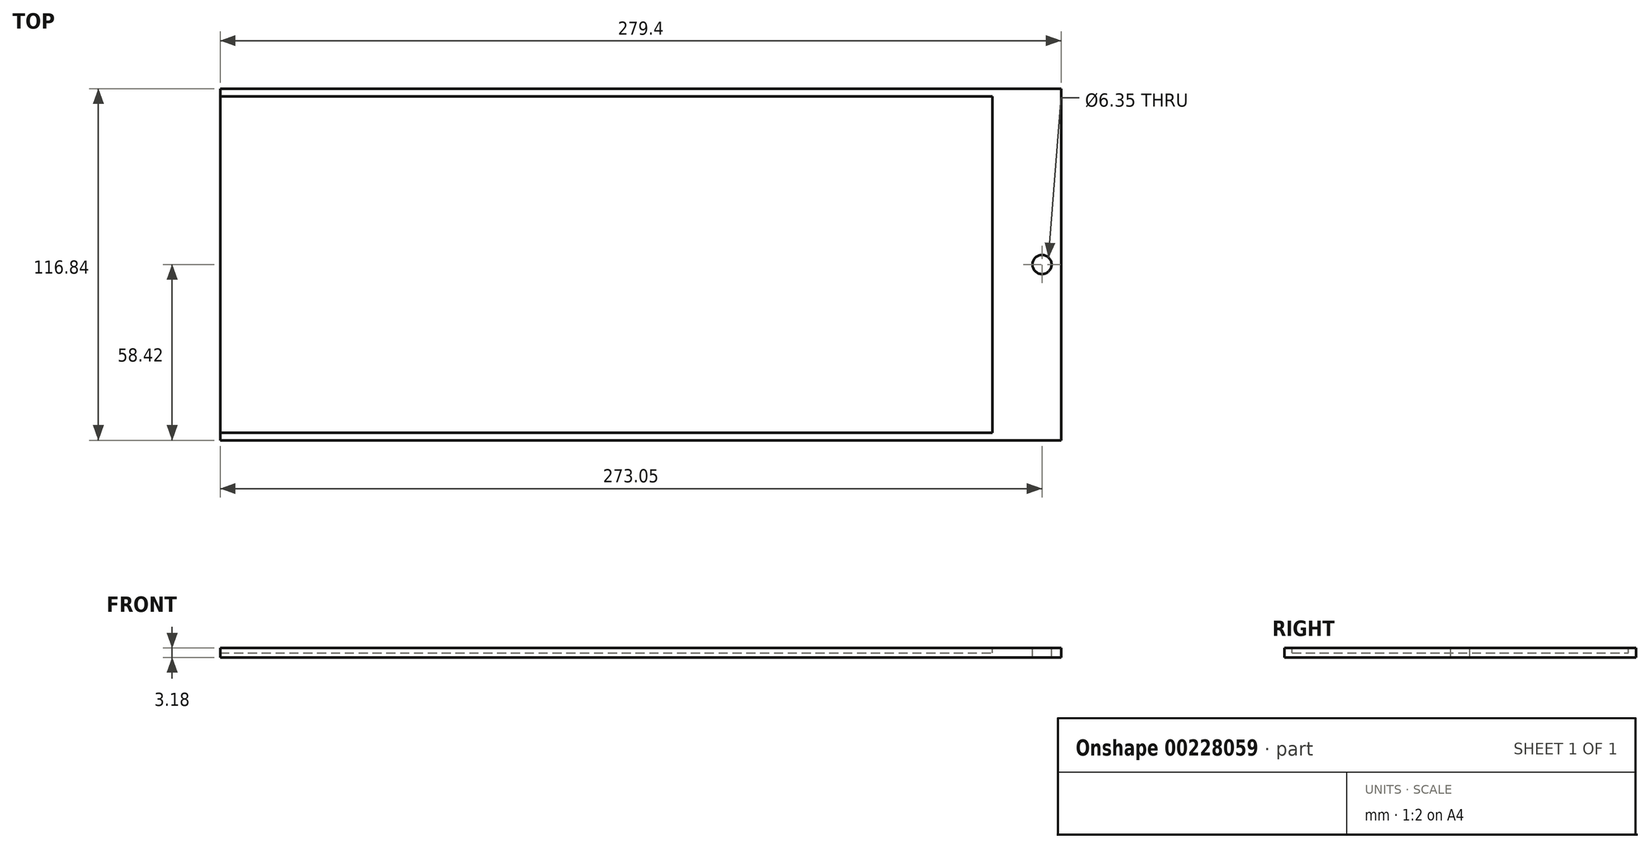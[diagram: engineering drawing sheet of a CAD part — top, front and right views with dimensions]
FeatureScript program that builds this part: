
annotation { "Feature Type Name" : "Feature", "Feature Type Description" : "" }
export const myFeature = defineFeature(function(context is Context, id is Id, definition is map)
    precondition{}
    {
        {
            var Q0;
            Q0=qCreatedBy(makeId("Top.planeOp"),FACE);
            var sketch = newSketch(context, id + "F0", { "sketchPlane" : qUnion([Q0])});
            skLineSegment(sketch, "E0.bottom", {"start": v(0, 0) * mm, "end": v(279.4, 0) * mm});
            skLineSegment(sketch, "E0.top", {"start": v(0, 116.84) * mm, "end": v(279.4, 116.84) * mm});
            skLineSegment(sketch, "E0.left", {"start": v(0, 0) * mm, "end": v(0, 116.84) * mm});
            skLineSegment(sketch, "E0.right", {"start": v(279.4, 0) * mm, "end": v(279.4, 116.84) * mm});
            skSolve(sketch);
        }
        {
            var Q0;
            Q0 = qSketchRegion(id + "F0", true);
            extrude(context, id + "F1", {"entities" : qUnion([Q0]), "depth" : 3.17 * mm, "offsetDistance" : 25.4 * mm});
        }
        {
            var Q0;
            Q0=makeQuery(id+"F1.opExtrude","CAP_FACE",FACE,{"disambiguationData":[OSD([sQuery(id+"F0.wireOp",EDGE,"E0.bottom"),sQuery(id+"F0.wireOp",EDGE,"E0.top"),sQuery(id+"F0.wireOp",EDGE,"E0.left"),sQuery(id+"F0.wireOp",EDGE,"E0.right")])],"isStart":false});
            var sketch = newSketch(context, id + "F2", { "sketchPlane" : qUnion([Q0])});
            skCircle(sketch, "E1", {"center": v(273.05, 58.42) * mm, "radius": 3.18 * mm});
            skLineSegment(sketch, "E2", {"start": v(279.4, 58.42) * mm, "end": v(0, 58.42) * mm, "construction": true});
            skSolve(sketch);
        }
        {
            var Q0;
            Q0 = qSketchRegion(id + "F2", true);
            extrude(context, id + "F3", {"entities" : qUnion([Q0]), "operationType" : NewBodyOperationType.REMOVE, "endBound" : BoundingType.THROUGH_ALL, "oppositeDirection" : true, "depth" : 25.4 * mm, "offsetDistance" : 25.4 * mm});
        }
        {
            var Q0;
            Q0=makeQuery(id+"F1.opExtrude","CAP_FACE",FACE,{"disambiguationData":[OSD([sQuery(id+"F0.wireOp",EDGE,"E0.bottom"),sQuery(id+"F0.wireOp",EDGE,"E0.top"),sQuery(id+"F0.wireOp",EDGE,"E0.left"),sQuery(id+"F0.wireOp",EDGE,"E0.right")])],"isStart":false});
            var sketch = newSketch(context, id + "F4", { "sketchPlane" : qUnion([Q0])});
            skLineSegment(sketch, "E3.bottom", {"start": v(0, 2.54) * mm, "end": v(256.54, 2.54) * mm});
            skLineSegment(sketch, "E3.top", {"start": v(0, 114.3) * mm, "end": v(256.54, 114.3) * mm});
            skLineSegment(sketch, "E3.left", {"start": v(0, 2.54) * mm, "end": v(0, 114.3) * mm});
            skLineSegment(sketch, "E3.right", {"start": v(256.54, 2.54) * mm, "end": v(256.54, 114.3) * mm});
            skLineSegment(sketch, "E4", {"start": v(279.4, 116.84) * mm, "end": v(256.54, 114.3) * mm, "construction": true});
            skLineSegment(sketch, "E5", {"start": v(256.54, 2.54) * mm, "end": v(279.4, 0) * mm, "construction": true});
            skSolve(sketch);
        }
        {
            var Q0;
            Q0 = qSketchRegion(id + "F4", true);
            extrude(context, id + "F5", {"entities" : qUnion([Q0]), "operationType" : NewBodyOperationType.REMOVE, "oppositeDirection" : true, "depth" : 1.59 * mm, "offsetDistance" : 25.4 * mm});
        }
        {
            var Q0;
            Q0 = qSketchRegion(id + "F4", true);
            extrude(context, id + "F6", {"entities" : qUnion([Q0]), "oppositeDirection" : true, "depth" : 1.59 * mm, "offsetDistance" : 25.4 * mm});
        }
    });
